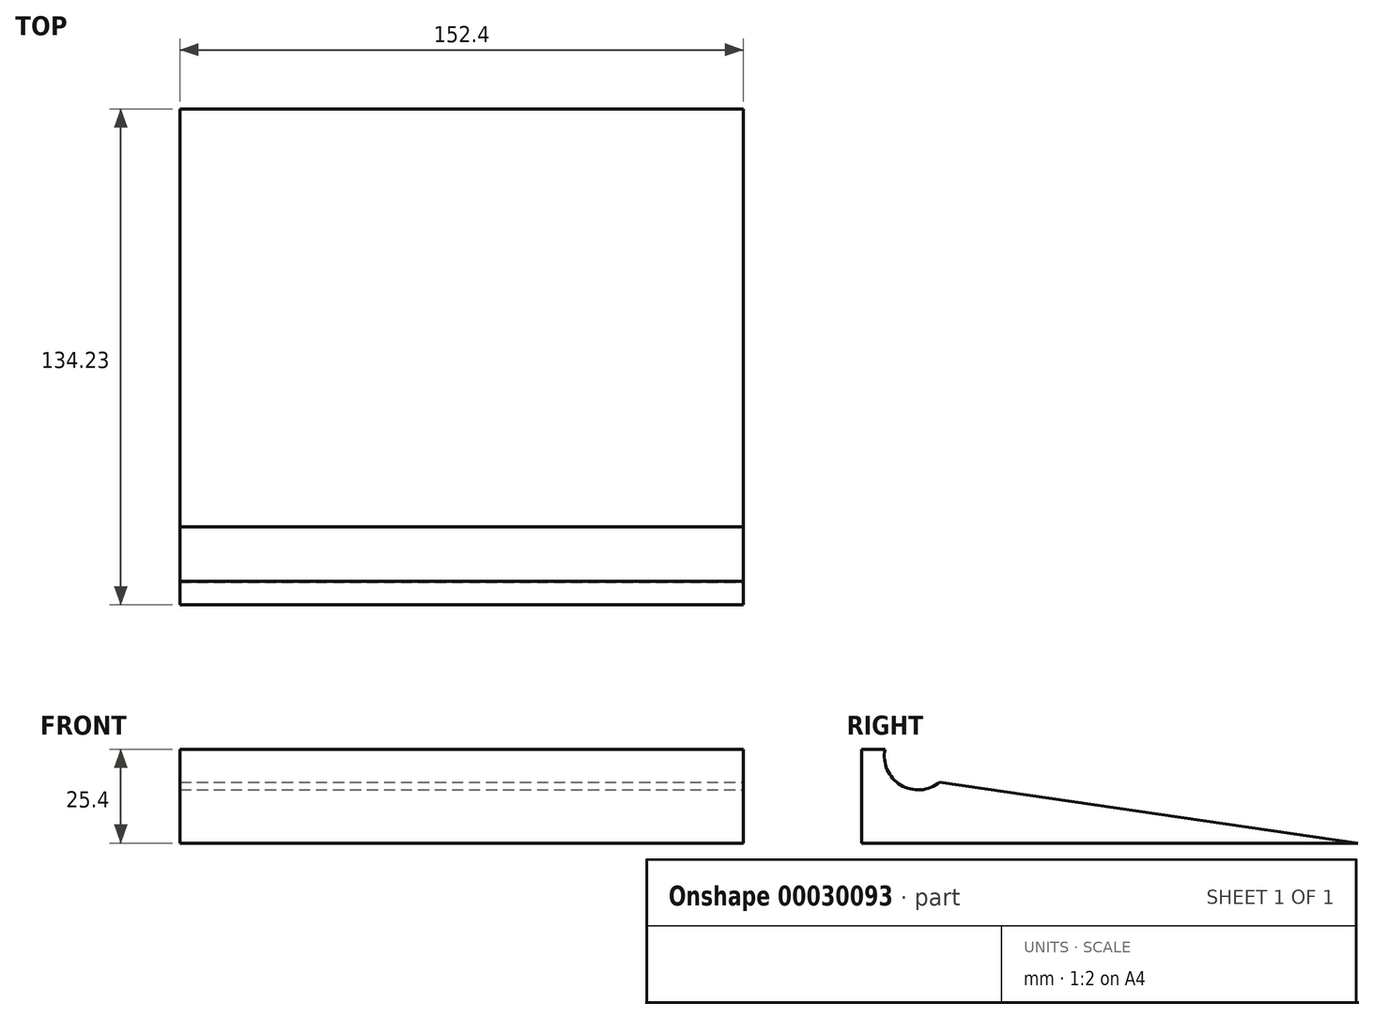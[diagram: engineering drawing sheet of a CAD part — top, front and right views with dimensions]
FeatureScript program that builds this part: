
annotation { "Feature Type Name" : "Feature", "Feature Type Description" : "" }
export const myFeature = defineFeature(function(context is Context, id is Id, definition is map)
    precondition{}
    {
        {
            var Q0;
            Q0=qCreatedBy(makeId("Right.planeOp"),FACE);
            var sketch = newSketch(context, id + "F0", { "sketchPlane" : qUnion([Q0])});
            skLineSegment(sketch, "E0", {"start": v(-90.45, 0.6) * mm, "end": v(41.63, 0.6) * mm});
            skArc(sketch, "E1", {"start": v(-86.25, 26) * mm, "mid": v(-82.03, 16.3) * mm, "end": v(-71.48, 17.07) * mm});
            skLineSegment(sketch, "E2", {"start": v(-71.48, 17.07) * mm, "end": v(41.63, 0.6) * mm});
            skLineSegment(sketch, "E3", {"start": v(-86.25, 26) * mm, "end": v(-92.6, 26) * mm});
            skLineSegment(sketch, "E4", {"start": v(-90.45, 0.6) * mm, "end": v(-92.6, 0.6) * mm});
            skLineSegment(sketch, "E5", {"start": v(-92.6, 0.6) * mm, "end": v(-92.6, 26) * mm});
            skSolve(sketch);
        }
        {
            var Q0;
            Q0=makeQuery(id+"F0.imprint","IMPRINT",FACE,{"disambiguationData":[TD([[makeQuery(id+"F0.imprint","IMPRINT",EDGE,{"derivedFrom":sQuery(id+"F0.wireOp",EDGE,"E0")}),1.0]])]});
            extrude(context, id + "F1", {"entities" : qUnion([Q0]), "oppositeDirection" : true, "depth" : 152.4 * mm});
        }
    });
